# Revit family: AZ-V2500BM5AHZF_()0000035069_Facebased_ver-2-0_2022________
name_source: partatom
category: 照明器具
units: mm (PartAtom-declared; Revit-internal decimal feet)

## family parameters
パーツ タイプ = 標準
ホスト = 面
ロード時にボイドで切り取り = はい
丸型コネクタ寸法 = 直径を使用
光源 = はい
共有 = いいえ
注釈の向きを維持 = いいえ
部屋計算ポイント = いいえ

## types (4) — shared parameters
Depth = 657  [stored 2.15551 ft]
Height = 136  [stored 0.446194 ft]
IfcExportAs = IfcLightFixtureType
LED制御装置 = 一般形(LN)
URL = https://www.mitsubishielectric.co.jp
Width = 657  [stored 2.15551 ft]
カラー フィルタ = 16777215
サービススペース = いいえ
モデル = AZ-V2500BM/5 AHZF
ランプ_全光束 = 0 lm
ランプ_定格消費電力 = 0.0 W
ランプ_電流 = 0.000 A
レンダリング時に放射形状を表示 = はい
企業コード = 118713
保守率(1)良いのコメント = 保守率良いの場合：0.77
保守率(2)普通のコメント = 保守率普通の場合：0.72
保守率(3)悪いのコメント = 保守率悪いの場合：0.68
傾斜角 = -90.00°
入力電圧1(電圧指定=1) = 100 V
入力電圧2(電圧指定=2) = 200 V
入力電圧3(電圧指定=3) = 242 V
分類コード = 40300000000000
周波数 = 0 Hz
呼称 = 青空照明 misola
安定器_二次電圧 = 0 V
安定器_入力電力 = 0.0 W
安定器_入力電流 = 0.000 A
安定器_定格電圧 = 0 V
定格入力電圧 = 100 V
形式 = 壁埋込
既定の高さ = 1219
材質_カバー = <カテゴリ別>
材質_ルーバー = <カテゴリ別>
材質_反射板 = <カテゴリ別>
材質_本体 = <カテゴリ別>
極数 = 1
相 = 1
積算_科目 = 1 電灯設備
製品質量 = 0.00 kg
製造元 = 三菱電機照明株式会社
設置方法 = 埋込
調光ランプの色温度変化。 = <なし>
質量 = 0.00 kg
運転質量 = 0.00 kg
長方形の幅に沿って放射 = 657  [stored 2.15551 ft]
長方形の長さに沿って放射 = 657  [stored 2.15551 ft]
開口部寸法(奥行) = 636  [stored 2.08661 ft]
開口部寸法(幅) = 636  [stored 2.08661 ft]
電圧指定 = 1
zero-valued in all types: Clearance Back, Clearance Bottom, Clearance Front, Clearance Left, Clearance Right, Clearance Top, ランプ_定格消費効率(lm/W), ランプ_本数, 直径, 配光角, 開口部寸法(径)

## per-type parameters (varying)
| type | コンバート開始日時 | フォトメトリック Web ファイル | 入力電流1 | 入力電流2 | 入力電流3 | 固有エネルギー消費効率(lm/W) | 定格光束 | 定格入力容量 | 定格入力電流 | 定格消費電力 | 平均演色評価数(Ra) | 消費電力1 | 消費電力2 | 消費電力3 | 皮相負荷 |
| _段調光_初期照度補正機能搭載なし_移ろう空　朝夕_ | 2023年10月06日(金) 16時56分55秒735 | AZ-V2500BM5AHZF_()0000035069_________DANCHO_-_ASAYU__.ies | 0.330 A | 0.170 A | 0.150 A | 39.506173 | 1280 lm | 33 VA | 0.330 A | 32.4 W | 0 | 32.4 W | 32.3 W | 32.5 W | 33 VA |
| _段調光_初期照度補正機能搭載なし_海の昼空*フレーム部100%_ | 2023年10月06日(金) 16時56分59秒044 | AZ-V2500BM5AHZF_()0000035072_________DANCHO_-_UMIHIRU100__.ies | 0.640 A | 0.320 A | 0.270 A | 39.68254 | 2500 lm | 64 VA | 0.640 A | 63.0 W | 83 | 63.0 W | 62.0 W | 62.0 W | 64 VA |
| _段調光_初期照度補正機能搭載なし_森の昼空*フレーム部100%_ | 2023年10月06日(金) 16時56分57秒387 | AZ-V2500BM5AHZF_()0000035068_________DANCHO_-_MORIHIRU100__.ies | 0.600 A | 0.300 A | 0.250 A | 42.22973 | 2500 lm | 60 VA | 0.600 A | 59.2 W | 83 | 59.2 W | 58.3 W | 58.3 W | 60 VA |
| _段調光_初期照度補正機能搭載なし_移ろう空　夜_ | 2023年10月06日(金) 16時56分54秒049 | AZ-V2500BM5AHZF_()0000035075_________DANCHO_-_YORU__.ies | 0.100 A | 0.070 A | 0.070 A | 14.065934 | 128 lm | 10 VA | 0.100 A | 9.1 W | 0 | 9.1 W | 9.7 W | 10.0 W | 10 VA |

note: [stored X ft] marks values corroborated as IEEE doubles in the binary element streams (Revit-internal decimal feet)
